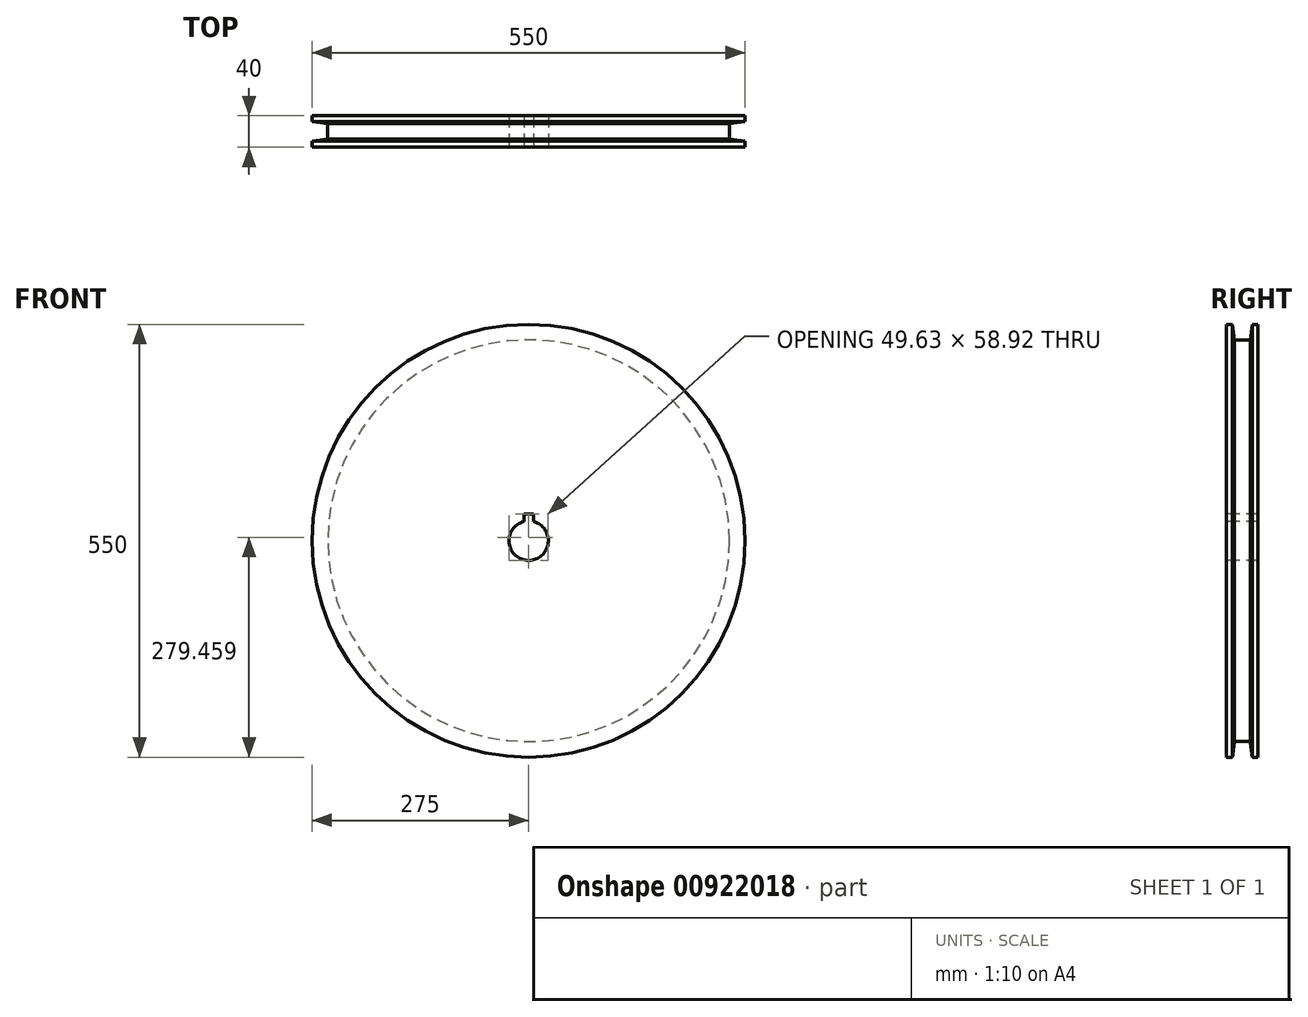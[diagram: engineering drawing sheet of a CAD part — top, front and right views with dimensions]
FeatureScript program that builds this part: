
annotation { "Feature Type Name" : "Feature", "Feature Type Description" : "" }
export const myFeature = defineFeature(function(context is Context, id is Id, definition is map)
    precondition{}
    {
        {
            var Q0;
            Q0=qCreatedBy(makeId("Right.planeOp"),FACE);
            var sketch = newSketch(context, id + "F0", { "sketchPlane" : qUnion([Q0])});
            skLineSegment(sketch, "E0.bottom", {"start": v(0, 25) * mm, "end": v(-20, 25) * mm});
            skLineSegment(sketch, "E0.top", {"start": v(-12.56, 275) * mm, "end": v(-20, 275) * mm});
            skLineSegment(sketch, "E0.right", {"start": v(-20, 25) * mm, "end": v(-20, 275) * mm});
            skLineSegment(sketch, "E1", {"start": v(-12.56, 275) * mm, "end": v(-10, 255.16) * mm});
            skLineSegment(sketch, "E2", {"start": v(-10, 255.16) * mm, "end": v(0, 255.16) * mm});
            skLineSegment(sketch, "E3", {"start": v(0, 0) * mm, "end": v(0, 25) * mm});
            skLineSegment(sketch, "E4.MirrorCS", {"start": v(10, 255.16) * mm, "end": v(0, 255.16) * mm});
            skLineSegment(sketch, "E5.MirrorCS", {"start": v(12.56, 275) * mm, "end": v(10, 255.16) * mm});
            skLineSegment(sketch, "E6.MirrorCS", {"start": v(20, 25) * mm, "end": v(20, 275) * mm});
            skLineSegment(sketch, "E7.MirrorCS", {"start": v(12.56, 275) * mm, "end": v(20, 275) * mm});
            skLineSegment(sketch, "E8.MirrorCS", {"start": v(0, 25) * mm, "end": v(20, 25) * mm});
            skLineSegment(sketch, "E9", {"start": v(-47.31, 0) * mm, "end": v(47.82, 0) * mm});
            skSolve(sketch);
        }
        {
            var Q0;
            Q0 = qSketchRegion(id + "F0", true);
            var Q1;
            Q1=sQuery(id+"F0.wireOp",EDGE,"E9");
            revolve(context, id + "F1", {"surfaceOperationType" : NewSurfaceOperationType.NEW, "entities" : qUnion([Q0]), "axis" : qUnion([Q1]), "revolveType" : RevolveType.FULL});
        }
        {
            var Q0;
            Q0=makeQuery(id+"F1.opRevolve","SWEPT_FACE",FACE,{"disambiguationData":[OSD([sQuery(id+"F0.wireOp",EDGE,"E0.right")])]});
            var sketch = newSketch(context, id + "F2", { "sketchPlane" : qUnion([Q0])});
            skLineSegment(sketch, "E10.bottom", {"start": v(-6, 33.92) * mm, "end": v(0, 33.92) * mm});
            skLineSegment(sketch, "E10.top", {"start": v(-6, 23.92) * mm, "end": v(0, 23.92) * mm});
            skLineSegment(sketch, "E10.left", {"start": v(-6, 33.92) * mm, "end": v(-6, 23.92) * mm});
            skLineSegment(sketch, "E11.MirrorCS", {"start": v(6, 33.92) * mm, "end": v(0, 33.92) * mm});
            skLineSegment(sketch, "E12.MirrorCS", {"start": v(6, 33.92) * mm, "end": v(6, 23.92) * mm});
            skLineSegment(sketch, "E13.MirrorCS", {"start": v(6, 23.92) * mm, "end": v(0, 23.92) * mm});
            skSolve(sketch);
        }
        {
            var Q0;
            Q0 = qSketchRegion(id + "F2", true);
            extrude(context, id + "F3", {"entities" : qUnion([Q0]), "operationType" : NewBodyOperationType.REMOVE, "endBound" : BoundingType.THROUGH_ALL, "oppositeDirection" : true, "depth" : 50 * mm, "offsetDistance" : 25 * mm});
        }
    });
